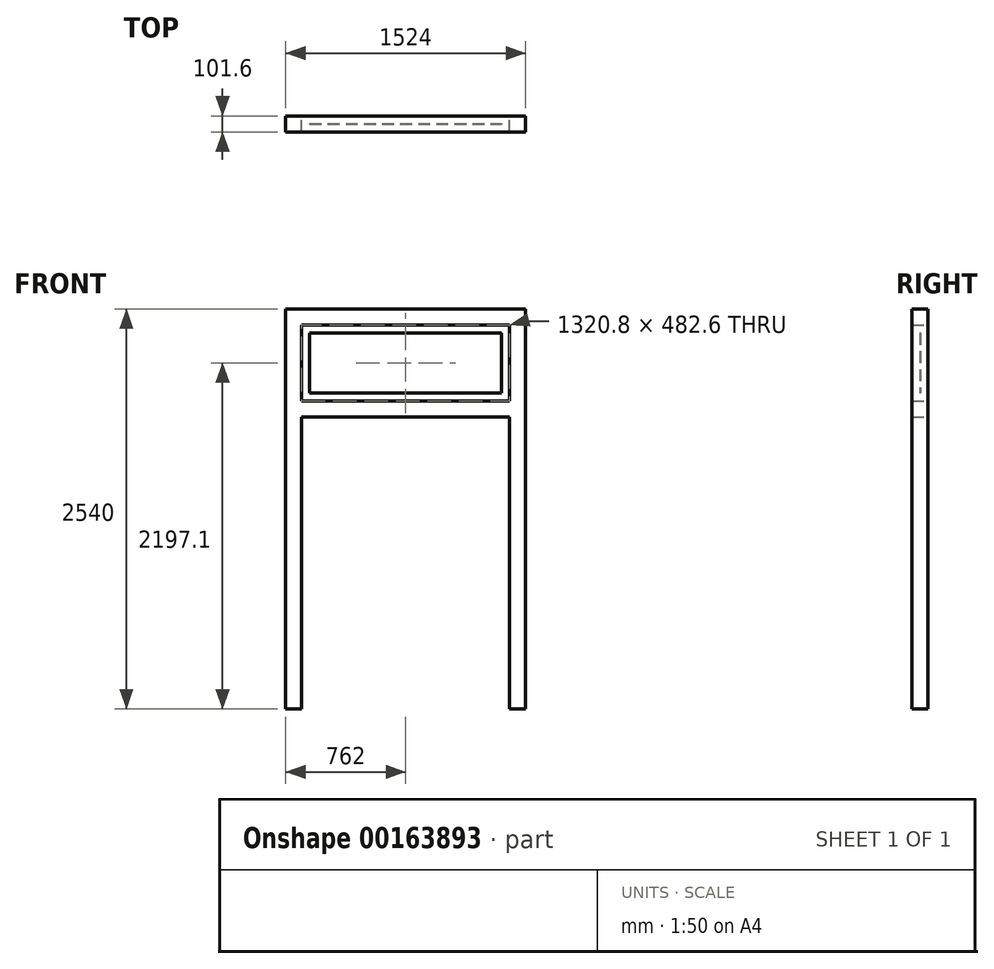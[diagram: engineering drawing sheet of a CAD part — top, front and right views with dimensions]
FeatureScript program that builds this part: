
annotation { "Feature Type Name" : "Feature", "Feature Type Description" : "" }
export const myFeature = defineFeature(function(context is Context, id is Id, definition is map)
    precondition{}
    {
        {
            var Q0;
            Q0=qCreatedBy(makeId("Front.planeOp"),FACE);
            var sketch = newSketch(context, id + "F0", { "sketchPlane" : qUnion([Q0])});
            skLineSegment(sketch, "E0", {"start": v(762, 1625.6) * mm, "end": v(762, -914.4) * mm});
            skLineSegment(sketch, "E1", {"start": v(762, -914.4) * mm, "end": v(660.4, -914.4) * mm});
            skLineSegment(sketch, "E2", {"start": v(660.4, 1524) * mm, "end": v(660.4, 1041.4) * mm});
            skLineSegment(sketch, "E3", {"start": v(660.4, 939.8) * mm, "end": v(660.4, -914.4) * mm});
            skLineSegment(sketch, "E4.MirrorCS", {"start": v(-762, 1625.6) * mm, "end": v(-762, -914.4) * mm});
            skLineSegment(sketch, "E5.MirrorCS", {"start": v(-660.4, 1524) * mm, "end": v(-660.4, 1041.4) * mm});
            skLineSegment(sketch, "E6.MirrorCS", {"start": v(-660.4, 939.8) * mm, "end": v(-660.4, -914.4) * mm});
            skLineSegment(sketch, "E7.MirrorCS", {"start": v(-762, -914.4) * mm, "end": v(-660.4, -914.4) * mm});
            skLineSegment(sketch, "E8", {"start": v(-762, 1625.6) * mm, "end": v(762, 1625.6) * mm});
            skLineSegment(sketch, "E9", {"start": v(660.4, 1524) * mm, "end": v(-660.4, 1524) * mm});
            skLineSegment(sketch, "E10", {"start": v(-660.4, 1041.4) * mm, "end": v(660.4, 1041.4) * mm});
            skLineSegment(sketch, "E11", {"start": v(660.4, 939.8) * mm, "end": v(-660.4, 939.8) * mm});
            skSolve(sketch);
        }
        {
            var Q0;
            Q0 = qSketchRegion(id + "F0", true);
            extrude(context, id + "F1", {"entities" : qUnion([Q0]), "endBound" : BoundingType.SYMMETRIC, "depth" : 101.6 * mm});
        }
        {
            var Q0;
            Q0=qCreatedBy(makeId("Front.planeOp"),FACE);
            var sketch = newSketch(context, id + "F2", { "sketchPlane" : qUnion([Q0])});
            skLineSegment(sketch, "E12.bottom", {"start": v(-609.6, 1473.2) * mm, "end": v(609.6, 1473.2) * mm});
            skLineSegment(sketch, "E12.top", {"start": v(-609.6, 1092.2) * mm, "end": v(609.6, 1092.2) * mm});
            skLineSegment(sketch, "E12.left", {"start": v(-609.6, 1473.2) * mm, "end": v(-609.6, 1092.2) * mm});
            skLineSegment(sketch, "E12.right", {"start": v(609.6, 1473.2) * mm, "end": v(609.6, 1092.2) * mm});
            skSolve(sketch);
        }
        {
            var Q0;
            Q0 = qSketchRegion(id + "F2", true);
            extrude(context, id + "F3", {"entities" : qUnion([Q0]), "endBound" : BoundingType.SYMMETRIC, "oppositeDirection" : true, "depth" : 3.17 * mm});
        }
    });
